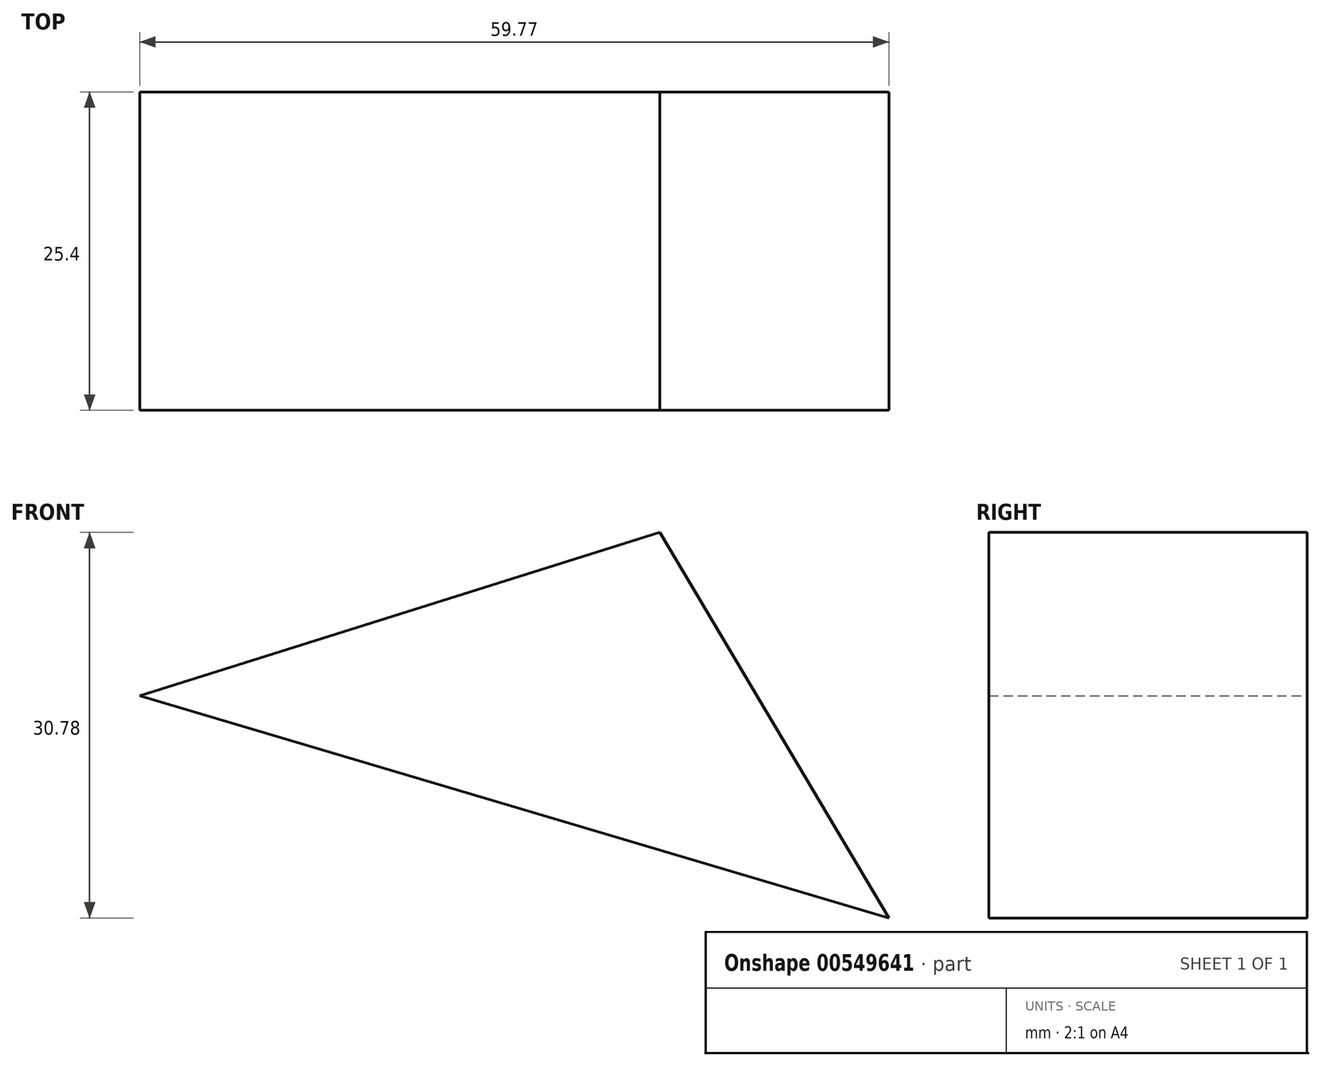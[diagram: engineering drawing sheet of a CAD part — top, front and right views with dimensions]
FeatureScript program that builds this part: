
annotation { "Feature Type Name" : "Feature", "Feature Type Description" : "" }
export const myFeature = defineFeature(function(context is Context, id is Id, definition is map)
    precondition{}
    {
        {
            var Q0;
            Q0=qCreatedBy(makeId("Front.planeOp"),FACE);
            var sketch = newSketch(context, id + "F0", { "sketchPlane" : qUnion([Q0])});
            skLineSegment(sketch, "E0", {"start": v(41.49, 13.05) * mm, "end": v(0, 0) * mm});
            skLineSegment(sketch, "E1", {"start": v(0, 0) * mm, "end": v(59.77, -17.73) * mm});
            skLineSegment(sketch, "E2", {"start": v(59.77, -17.73) * mm, "end": v(41.49, 13.05) * mm});
            skSolve(sketch);
        }
        {
            var Q0;
            Q0 = qSketchRegion(id + "F0", true);
            var Q1;
            Q1=makeQuery(id+"F0.imprint","IMPRINT",FACE,{"disambiguationData":[TD([[makeQuery(id+"F0.imprint","IMPRINT",EDGE,{"derivedFrom":sQuery(id+"F0.wireOp",EDGE,"E0")}),1.0]])]});
            extrude(context, id + "F1", {"entities" : qUnion([Q0, Q1]), "depth" : 25.4 * mm, "offsetDistance" : 25.4 * mm});
        }
    });
